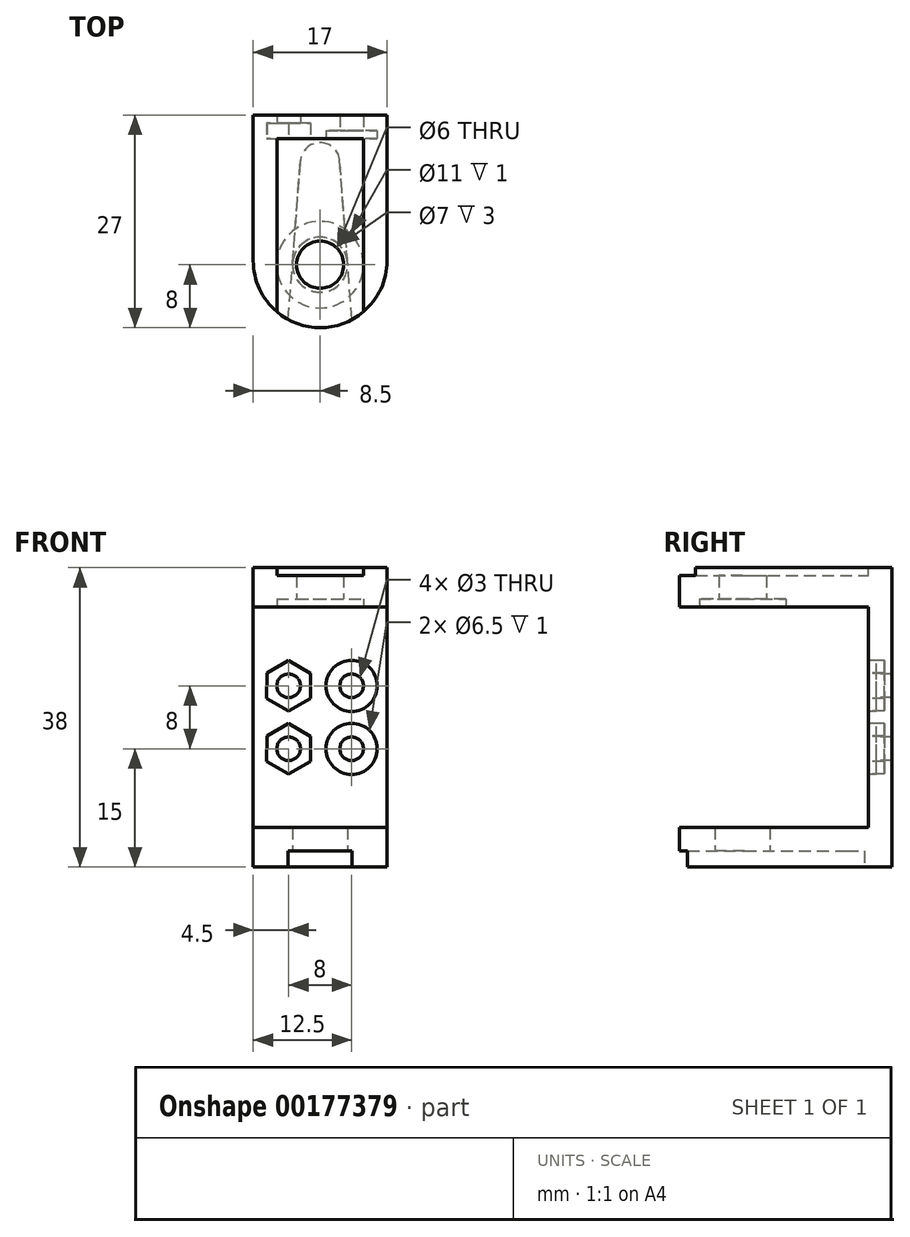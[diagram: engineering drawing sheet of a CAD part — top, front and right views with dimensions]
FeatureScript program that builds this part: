
annotation { "Feature Type Name" : "Feature", "Feature Type Description" : "" }
export const myFeature = defineFeature(function(context is Context, id is Id, definition is map)
    precondition{}
    {
        {
            var Q0;
            Q0=qCreatedBy(makeId("Front.planeOp"),FACE);
            var sketch = newSketch(context, id + "F0", { "sketchPlane" : qUnion([Q0])});
            skLineSegment(sketch, "E0.bottom", {"start": v(8.5, 19) * mm, "end": v(-8.5, 19) * mm});
            skLineSegment(sketch, "E0.top", {"start": v(8.5, -19) * mm, "end": v(-8.5, -19) * mm});
            skLineSegment(sketch, "E0.left", {"start": v(8.5, 19) * mm, "end": v(8.5, -19) * mm});
            skLineSegment(sketch, "E0.right", {"start": v(-8.5, 19) * mm, "end": v(-8.5, -19) * mm});
            skPoint(sketch, "E0.middle", {"position": v(0, 0) * mm});
            skSolve(sketch);
        }
        {
            var Q0;
            Q0=qSketchRegion(id+"F0",true);
            extrude(context, id + "F1", {"entities" : qUnion([Q0]), "depth" : 3 * mm});
        }
        {
            var Q0;
            Q0=makeQuery(id+"F1.opExtrude","CAP_FACE",FACE,{"disambiguationData":[OSD([sQuery(id+"F0.wireOp",EDGE,"E0.bottom"),sQuery(id+"F0.wireOp",EDGE,"E0.top"),sQuery(id+"F0.wireOp",EDGE,"E0.left"),sQuery(id+"F0.wireOp",EDGE,"E0.right")])],"isStart":false});
            var sketch = newSketch(context, id + "F2", { "sketchPlane" : qUnion([Q0])});
            skLineSegment(sketch, "E1.bottom", {"start": v(-8.5, -19) * mm, "end": v(8.5, -19) * mm});
            skLineSegment(sketch, "E1.top", {"start": v(-8.5, -14) * mm, "end": v(8.5, -14) * mm});
            skLineSegment(sketch, "E1.left", {"start": v(-8.5, -19) * mm, "end": v(-8.5, -14) * mm});
            skLineSegment(sketch, "E1.right", {"start": v(8.5, -19) * mm, "end": v(8.5, -14) * mm});
            skLineSegment(sketch, "E2.MirrorCS", {"start": v(-8.5, 14) * mm, "end": v(8.5, 14) * mm});
            skLineSegment(sketch, "E3.MirrorCS", {"start": v(-8.5, 19) * mm, "end": v(-8.5, 14) * mm});
            skLineSegment(sketch, "E4.MirrorCS", {"start": v(-8.5, 19) * mm, "end": v(8.5, 19) * mm});
            skLineSegment(sketch, "E5.MirrorCS", {"start": v(8.5, 19) * mm, "end": v(8.5, 14) * mm});
            skSolve(sketch);
        }
        {
            var Q0;
            Q0=qSketchRegion(id+"F2",true);
            extrude(context, id + "F3", {"entities" : qUnion([Q0]), "operationType" : NewBodyOperationType.ADD, "depth" : 24 * mm});
        }
        {
            var Q0;
            Q0=makeQuery(id+"F3.opExtrude","CAP_EDGE",EDGE,{"disambiguationData":[OSD([sQuery(id+"F2.wireOp",EDGE,"E1.right")])],"isStart":false});
            var Q1;
            Q1=makeQuery(id+"F3.opExtrude","CAP_EDGE",EDGE,{"disambiguationData":[OSD([sQuery(id+"F2.wireOp",EDGE,"E1.left")])],"isStart":false});
            var Q2;
            Q2=makeQuery(id+"F3.opExtrude","CAP_EDGE",EDGE,{"disambiguationData":[OSD([sQuery(id+"F2.wireOp",EDGE,"E5.MirrorCS")])],"isStart":false});
            var Q3;
            Q3=makeQuery(id+"F3.opExtrude","CAP_EDGE",EDGE,{"disambiguationData":[OSD([sQuery(id+"F2.wireOp",EDGE,"E3.MirrorCS")])],"isStart":false});
            fillet(context, id + "F4", {"entities" : qUnion([Q0, Q1, Q2, Q3]), "radius" : 8.5 * mm, "tangentPropagation" : true, "allowEdgeOverflow" : false});
        }
        {
            var Q0;
            Q0=makeQuery(id+"F3.boolean.opBoolean","MERGE",FACE,{"derivedFrom":[makeQuery(id+"F1.opExtrude","SWEPT_FACE",FACE,{"disambiguationData":[OSD([sQuery(id+"F0.wireOp",EDGE,"E0.top")])]}),makeQuery(id+"F3.opExtrude","SWEPT_FACE",FACE,{"disambiguationData":[OSD([sQuery(id+"F2.wireOp",EDGE,"E1.bottom")])]})]});
            var sketch = newSketch(context, id + "F5", { "sketchPlane" : qUnion([Q0])});
            skCircle(sketch, "E6", {"center": v(0, 19) * mm, "radius": 3 * mm});
            skSolve(sketch);
        }
        {
            var Q0;
            Q0=makeQuery(id+"F5.imprint","IMPRINT",FACE,{"disambiguationData":[TD([[makeQuery(id+"F5.imprint","IMPRINT",EDGE,{"derivedFrom":sQuery(id+"F5.wireOp",EDGE,"E6")}),1.0]])]});
            extrude(context, id + "F6", {"entities" : qUnion([Q0]), "operationType" : NewBodyOperationType.REMOVE, "oppositeDirection" : true, "depth" : 40 * mm});
        }
        {
            var Q0;
            Q0=makeQuery(id+"F3.boolean.opBoolean","MERGE",FACE,{"derivedFrom":[makeQuery(id+"F1.opExtrude","SWEPT_FACE",FACE,{"disambiguationData":[OSD([sQuery(id+"F0.wireOp",EDGE,"E0.bottom")])]}),makeQuery(id+"F3.opExtrude","SWEPT_FACE",FACE,{"disambiguationData":[OSD([sQuery(id+"F2.wireOp",EDGE,"E4.MirrorCS")])]})]});
            var sketch = newSketch(context, id + "F7", { "sketchPlane" : qUnion([Q0])});
            skLineSegment(sketch, "E7.bottom", {"start": v(5.5, -32.98) * mm, "end": v(-5.5, -32.98) * mm});
            skLineSegment(sketch, "E7.top", {"start": v(5.5, -3) * mm, "end": v(-5.5, -3) * mm});
            skLineSegment(sketch, "E7.left", {"start": v(5.5, -32.98) * mm, "end": v(5.5, -3) * mm});
            skLineSegment(sketch, "E7.right", {"start": v(-5.5, -32.98) * mm, "end": v(-5.5, -3) * mm});
            skSolve(sketch);
        }
        {
            var Q0;
            Q0=qSketchRegion(id+"F7",true);
            extrude(context, id + "F8", {"entities" : qUnion([Q0]), "operationType" : NewBodyOperationType.REMOVE, "oppositeDirection" : true, "depth" : 1 * mm});
        }
        {
            var Q0;
            Q0=makeQuery(id+"F3.boolean.opBoolean","MERGE",FACE,{"derivedFrom":[makeQuery(id+"F1.opExtrude","SWEPT_FACE",FACE,{"disambiguationData":[OSD([sQuery(id+"F0.wireOp",EDGE,"E0.top")])]}),makeQuery(id+"F3.opExtrude","SWEPT_FACE",FACE,{"disambiguationData":[OSD([sQuery(id+"F2.wireOp",EDGE,"E1.bottom")])]})]});
            var sketch = newSketch(context, id + "F9", { "sketchPlane" : qUnion([Q0])});
            skLineSegment(sketch, "E8", {"start": v(-4.23, 28.38) * mm, "end": v(-2.5, 5.8) * mm});
            skLineSegment(sketch, "E9.MirrorCS", {"start": v(4.23, 28.38) * mm, "end": v(2.5, 5.8) * mm});
            skArc(sketch, "E10", {"start": v(-2.5, 5.8) * mm, "mid": v(0, 3.5) * mm, "end": v(2.5, 5.8) * mm});
            skLineSegment(sketch, "E11", {"start": v(-4.23, 28.38) * mm, "end": v(4.23, 28.38) * mm});
            skCircle(sketch, "E12", {"center": v(0, 19) * mm, "radius": 3.5 * mm});
            skSolve(sketch);
        }
        {
            var Q0;
            Q0=qSketchRegion(id+"F9",true);
            extrude(context, id + "F10", {"entities" : qUnion([Q0]), "operationType" : NewBodyOperationType.REMOVE, "oppositeDirection" : true, "depth" : 2 * mm});
        }
        {
            var Q0;
            Q0=makeQuery(id+"F3.opExtrude","SWEPT_FACE",FACE,{"disambiguationData":[OSD([sQuery(id+"F2.wireOp",EDGE,"E2.MirrorCS")])]});
            var sketch = newSketch(context, id + "F11", { "sketchPlane" : qUnion([Q0])});
            skCircle(sketch, "E13", {"center": v(0, 19) * mm, "radius": 5.5 * mm});
            skSolve(sketch);
        }
        {
            var Q0;
            Q0=qSketchRegion(id+"F11",true);
            extrude(context, id + "F12", {"entities" : qUnion([Q0]), "operationType" : NewBodyOperationType.REMOVE, "oppositeDirection" : true, "depth" : 1 * mm});
        }
        {
            var Q0;
            Q0=makeQuery(id+"F1.opExtrude","CAP_FACE",FACE,{"disambiguationData":[OSD([sQuery(id+"F0.wireOp",EDGE,"E0.bottom"),sQuery(id+"F0.wireOp",EDGE,"E0.top"),sQuery(id+"F0.wireOp",EDGE,"E0.left"),sQuery(id+"F0.wireOp",EDGE,"E0.right")])],"isStart":true});
            var sketch = newSketch(context, id + "F13", { "sketchPlane" : qUnion([Q0])});
            skPoint(sketch, "E14", {"position": v(-4, -4) * mm});
            skPoint(sketch, "E15.MirrorP", {"position": v(-4, 4) * mm});
            skSolve(sketch);
        }
        {
            var Q0;
            Q0=sQuery(id+"F13.wireOp",VERTEX,"E15.MirrorP");
            var Q1;
            Q1=sQuery(id+"F13.wireOp",VERTEX,"5d9b686c-818d-4e17-add7-60bd97503a200.MirrorP");
            var Q2;
            Q2=sQuery(id+"F13.wireOp",VERTEX,"E14");
            var Q3;
            Q3=sQuery(id+"F13.wireOp",VERTEX,"a18d2e19-8ac6-4625-9ebd-ed48deb488a20.MirrorP");
            var Q4;
            Q4=makeQuery(id+"F1.opExtrude","SWEPT_BODY",BODY,{"disambiguationData":[OSD([sQuery(id+"F0.wireOp",EDGE,"E0.bottom"),sQuery(id+"F0.wireOp",EDGE,"E0.top"),sQuery(id+"F0.wireOp",EDGE,"E0.left"),sQuery(id+"F0.wireOp",EDGE,"E0.right")])]});
            hole(context, id + "F14", {"style" : HoleStyle.SIMPLE, "endStyle" : HoleEndStyle.BLIND, "holeDiameter" : 1 * mm, "holeDepth" : 20 * mm, "startFromSketch" : true, "locations" : qUnion([Q0, Q1, Q2, Q3]), "scope" : qUnion([Q4])});
        }
        {
            var Q0;
            Q0=makeQuery(id+"F1.opExtrude","CAP_FACE",FACE,{"disambiguationData":[OSD([sQuery(id+"F0.wireOp",EDGE,"E0.bottom"),sQuery(id+"F0.wireOp",EDGE,"E0.top"),sQuery(id+"F0.wireOp",EDGE,"E0.left"),sQuery(id+"F0.wireOp",EDGE,"E0.right")])],"isStart":false});
            var sketch = newSketch(context, id + "F15", { "sketchPlane" : qUnion([Q0])});
            skPoint(sketch, "E16", {"position": v(4, 4) * mm});
            skPoint(sketch, "E17", {"position": v(4, -4) * mm});
            skPoint(sketch, "E18", {"position": v(-4, -4) * mm});
            skSolve(sketch);
        }
        {
            var Q0;
            Q0=sQuery(id+"F15.wireOp",VERTEX,"1e0347c8-6699-4331-95e7-cd0aa3de58a7");
            var Q1;
            Q1=sQuery(id+"F15.wireOp",VERTEX,"E16");
            var Q2;
            Q2=sQuery(id+"F15.wireOp",VERTEX,"E17");
            var Q3;
            Q3=makeQuery(id+"F1.opExtrude","SWEPT_BODY",BODY,{"disambiguationData":[OSD([sQuery(id+"F0.wireOp",EDGE,"E0.bottom"),sQuery(id+"F0.wireOp",EDGE,"E0.top"),sQuery(id+"F0.wireOp",EDGE,"E0.left"),sQuery(id+"F0.wireOp",EDGE,"E0.right")])]});
            hole(context, id + "F16", {"style" : HoleStyle.C_BORE, "endStyle" : HoleEndStyle.BLIND, "holeDiameter" : 3 * mm, "cBoreDiameter" : 6.5 * mm, "cBoreDepth" : 1 * mm, "holeDepth" : 20 * mm, "startFromSketch" : true, "locations" : qUnion([Q0, Q1, Q2]), "scope" : qUnion([Q3])});
        }
        {
            var Q0;
            Q0=makeQuery(id+"F1.opExtrude","CAP_FACE",FACE,{"disambiguationData":[OSD([sQuery(id+"F0.wireOp",EDGE,"E0.bottom"),sQuery(id+"F0.wireOp",EDGE,"E0.top"),sQuery(id+"F0.wireOp",EDGE,"E0.left"),sQuery(id+"F0.wireOp",EDGE,"E0.right")])],"isStart":false});
            var sketch = newSketch(context, id + "F17", { "sketchPlane" : qUnion([Q0])});
            skSolve(sketch);
        }
        {
            var Q0;
            Q0=makeQuery(id+"F10.boolean.opBoolean","COPY",FACE,{"derivedFrom":makeQuery(id+"F10.opExtrude","CAP_FACE",FACE,{"disambiguationData":[OSD([sQuery(id+"F9.wireOp",EDGE,"E8"),sQuery(id+"F9.wireOp",EDGE,"E9.MirrorCS"),sQuery(id+"F9.wireOp",EDGE,"E10"),sQuery(id+"F9.wireOp",EDGE,"E11"),sQuery(id+"F9.wireOp",EDGE,"E12")])],"isStart":false})});
            var sketch = newSketch(context, id + "F18", { "sketchPlane" : qUnion([Q0])});
            skCircle(sketch, "E19", {"center": v(0, 19) * mm, "radius": 3.5 * mm});
            skSolve(sketch);
        }
        {
            var Q0;
            Q0=qSketchRegion(id+"F18",true);
            extrude(context, id + "F19", {"entities" : qUnion([Q0]), "operationType" : NewBodyOperationType.REMOVE, "oppositeDirection" : true, "depth" : 25 * mm});
        }
        {
            var Q0;
            Q0=makeQuery(id+"F17.imprint","IMPRINT",FACE,{"disambiguationData":[TD([[makeQuery(id+"F17.imprint","IMPRINT",EDGE,{"derivedFrom":makeQuery(id+"F1.opExtrude","CAP_EDGE",EDGE,{"disambiguationData":[OSD([sQuery(id+"F0.wireOp",EDGE,"E0.left")])],"isStart":false})}),-1.0]])]});
            var sketch = newSketch(context, id + "F20", { "sketchPlane" : qUnion([Q0])});
            skPoint(sketch, "E20", {"position": v(4, 4) * mm});
            skPoint(sketch, "E21", {"position": v(-4, 4) * mm});
            skPoint(sketch, "E22", {"position": v(4, -4) * mm});
            skPoint(sketch, "E23", {"position": v(-4, -4) * mm});
            skCircle(sketch, "E24.cCircle", {"center": v(-4, 4) * mm, "radius": 2.77 * mm, "construction": true});
            skLineSegment(sketch, "E24.0", {"start": v(-3.99, 7.2) * mm, "end": v(-1.22, 5.6) * mm});
            skLineSegment(sketch, "E24.1", {"start": v(-1.22, 5.6) * mm, "end": v(-1.23, 2.39) * mm});
            skLineSegment(sketch, "E24.2", {"start": v(-1.23, 2.39) * mm, "end": v(-4.01, 0.8) * mm});
            skLineSegment(sketch, "E24.3", {"start": v(-4.01, 0.8) * mm, "end": v(-6.78, 2.4) * mm});
            skLineSegment(sketch, "E24.4", {"start": v(-6.78, 2.4) * mm, "end": v(-6.77, 5.61) * mm});
            skLineSegment(sketch, "E24.5", {"start": v(-6.77, 5.61) * mm, "end": v(-3.99, 7.2) * mm});
            skPoint(sketch, "E24.0.midPoint", {"position": v(-2.6, 6.4) * mm});
            skCircle(sketch, "E25.cCircle", {"center": v(-4, -4) * mm, "radius": 2.78 * mm, "construction": true});
            skLineSegment(sketch, "E25.0", {"start": v(-3.99, -0.8) * mm, "end": v(-1.22, -2.4) * mm});
            skLineSegment(sketch, "E25.1", {"start": v(-1.22, -2.4) * mm, "end": v(-1.23, -5.61) * mm});
            skLineSegment(sketch, "E25.2", {"start": v(-1.23, -5.61) * mm, "end": v(-4.01, -7.2) * mm});
            skLineSegment(sketch, "E25.3", {"start": v(-4.01, -7.2) * mm, "end": v(-6.78, -5.6) * mm});
            skLineSegment(sketch, "E25.4", {"start": v(-6.78, -5.6) * mm, "end": v(-6.77, -2.39) * mm});
            skLineSegment(sketch, "E25.5", {"start": v(-6.77, -2.39) * mm, "end": v(-3.99, -0.8) * mm});
            skPoint(sketch, "E25.0.midPoint", {"position": v(-2.6, -1.6) * mm});
            skSolve(sketch);
        }
        {
            var Q0;
            Q0=qSketchRegion(id+"F20",true);
            extrude(context, id + "F21", {"entities" : qUnion([Q0]), "operationType" : NewBodyOperationType.REMOVE, "oppositeDirection" : true, "depth" : 2 * mm});
        }
        {
            var Q0;
            Q0=sQuery(id+"F20.wireOp",VERTEX,"E21");
            var Q1;
            Q1=sQuery(id+"F20.wireOp",VERTEX,"E23");
            var Q2;
            Q2=makeQuery(id+"F1.opExtrude","SWEPT_BODY",BODY,{"disambiguationData":[OSD([sQuery(id+"F0.wireOp",EDGE,"E0.bottom"),sQuery(id+"F0.wireOp",EDGE,"E0.top"),sQuery(id+"F0.wireOp",EDGE,"E0.left"),sQuery(id+"F0.wireOp",EDGE,"E0.right")])]});
            hole(context, id + "F22", {"style" : HoleStyle.SIMPLE, "endStyle" : HoleEndStyle.THROUGH, "holeDiameter" : 3 * mm, "startFromSketch" : true, "locations" : qUnion([Q0, Q1]), "scope" : qUnion([Q2]), "isTappedThrough" : true});
        }
    });
